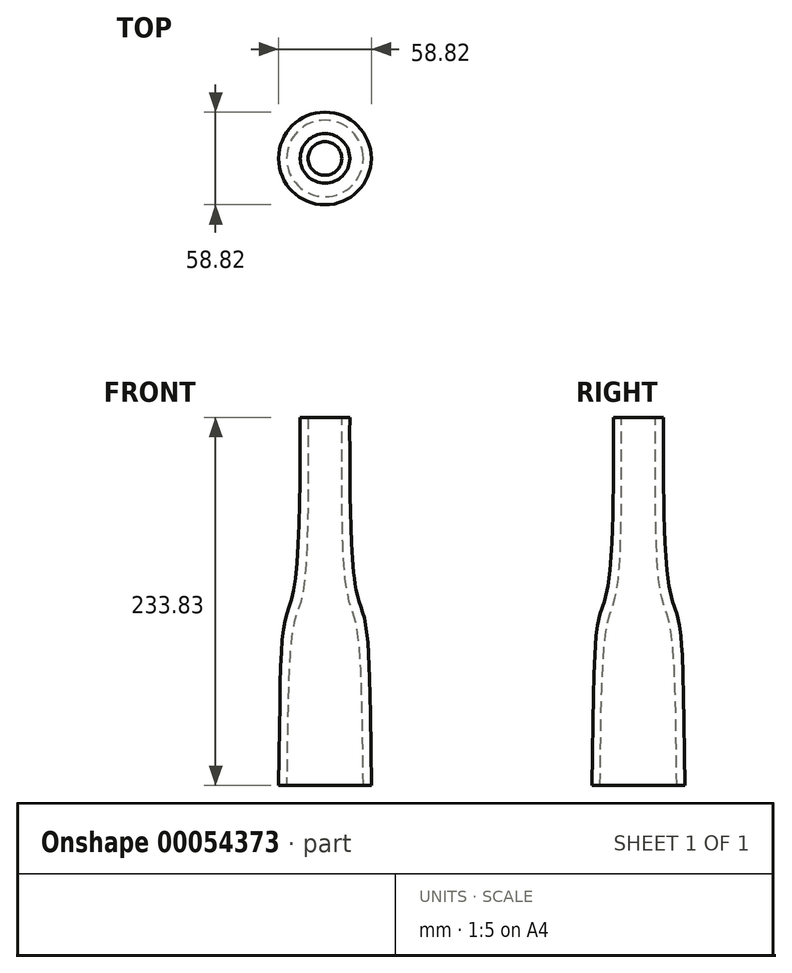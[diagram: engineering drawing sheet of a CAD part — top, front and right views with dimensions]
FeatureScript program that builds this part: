
annotation { "Feature Type Name" : "Feature", "Feature Type Description" : "" }
export const myFeature = defineFeature(function(context is Context, id is Id, definition is map)
    precondition{}
    {
        {
            var Q0;
            Q0=qCreatedBy(makeId("Right.planeOp"),FACE);
            var sketch = newSketch(context, id + "F0", { "sketchPlane" : qUnion([Q0])});
            skPoint(sketch, "E0", {"position": v(-10.67, 158.46) * mm});
            skPoint(sketch, "E1", {"position": v(-29.41, -75.37) * mm});
            skPoint(sketch, "E2", {"position": v(-15.75, 158.46) * mm});
            skPoint(sketch, "E3", {"position": v(-24.33, -75.37) * mm});
            skFitSpline(sketch, "E4", {"points": [v(-15.75, 158.46) * mm, v(-18.96, 53.91) * mm, v(-25.04, 30.8) * mm, v(-29.41, -75.37) * mm], "startDerivative": vector(-0.08, -136.8) * mm, "endDerivative": vector(-7.3, -477.82) * mm});
            skFitSpline(sketch, "E5", {"points": [v(-10.67, 158.46) * mm, v(-13.18, 52.47) * mm, v(-19.27, 29.35) * mm, v(-24.33, -75.37) * mm], "startDerivative": vector(-2.6, -144.62) * mm, "endDerivative": vector(-5.39, -450.97) * mm});
            skLineSegment(sketch, "E6", {"start": v(-15.75, 158.46) * mm, "end": v(-10.67, 158.46) * mm});
            skLineSegment(sketch, "E7", {"start": v(-29.41, -75.37) * mm, "end": v(-24.33, -75.37) * mm});
            skLineSegment(sketch, "E8", {"start": v(0, -146.99) * mm, "end": v(0, 178.23) * mm, "construction": true});
            skSolve(sketch);
        }
        {
            var Q0;
            Q0=makeQuery(id+"F0.imprint","IMPRINT",FACE,{"disambiguationData":[TD([[makeQuery(id+"F0.imprint","IMPRINT",EDGE,{"derivedFrom":sQuery(id+"F0.wireOp",EDGE,"E4")}),1.0]])]});
            var Q1;
            Q1=sQuery(id+"F0.wireOp",EDGE,"E8");
            revolve(context, id + "F1", {"entities" : qUnion([Q0]), "axis" : qUnion([Q1]), "revolveType" : RevolveType.FULL});
        }
    });
